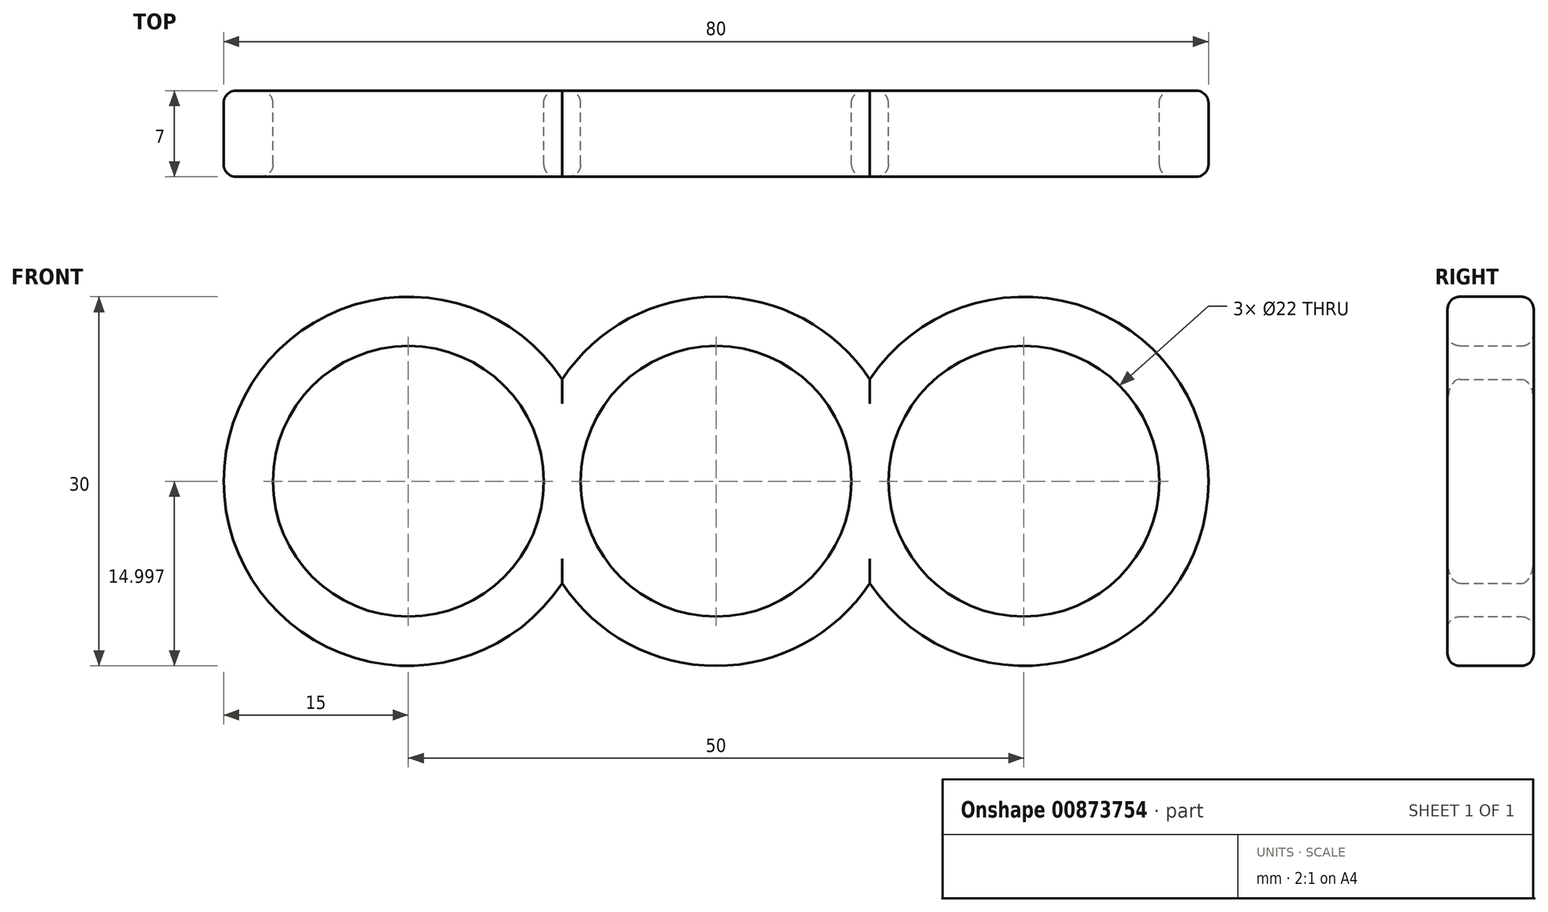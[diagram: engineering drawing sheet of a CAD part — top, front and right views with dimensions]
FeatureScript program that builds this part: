
annotation { "Feature Type Name" : "Feature", "Feature Type Description" : "" }
export const myFeature = defineFeature(function(context is Context, id is Id, definition is map)
    precondition{}
    {
        {
            var Q0;
            Q0=qCreatedBy(makeId("Front.planeOp"),FACE);
            var sketch = newSketch(context, id + "F0", { "sketchPlane" : qUnion([Q0])});
            skArc(sketch, "E0", {"start": v(0, 51.39) * mm, "mid": v(-11, 40.39) * mm, "end": v(0, 29.39) * mm});
            skArc(sketch, "E1", {"start": v(-12.5, 32.1) * mm, "mid": v(-7.1, 27.17) * mm, "end": v(0, 25.39) * mm});
            skCircle(sketch, "E2", {"center": v(-25, 40.39) * mm, "radius": 11 * mm});
            skArc(sketch, "E3", {"start": v(-12.5, 48.68) * mm, "mid": v(-40, 40.39) * mm, "end": v(-12.5, 32.1) * mm});
            skArc(sketch, "E4.trimOffspring", {"start": v(0, 55.39) * mm, "mid": v(-7.1, 53.6) * mm, "end": v(-12.5, 48.68) * mm});
            skArc(sketch, "E5.MirrorCS", {"start": v(0, 51.39) * mm, "mid": v(11, 40.39) * mm, "end": v(0, 29.39) * mm});
            skArc(sketch, "E6.MirrorCS", {"start": v(12.5, 32.1) * mm, "mid": v(7.1, 27.17) * mm, "end": v(0, 25.39) * mm});
            skArc(sketch, "E7.MirrorCS", {"start": v(0, 55.39) * mm, "mid": v(7.1, 53.6) * mm, "end": v(12.5, 48.68) * mm});
            skArc(sketch, "E8.MirrorCS", {"start": v(12.5, 48.68) * mm, "mid": v(40, 40.39) * mm, "end": v(12.5, 32.1) * mm});
            skCircle(sketch, "E9.MirrorC", {"center": v(25, 40.39) * mm, "radius": 11 * mm});
            skSolve(sketch);
        }
        {
            var Q0;
            Q0 = qSketchRegion(id + "F0", true);
            extrude(context, id + "F1", {"entities" : qUnion([Q0]), "depth" : 7 * mm, "offsetDistance" : 25 * mm});
        }
        {
            var Q0;
            Q0=makeQuery(id+"F1.opExtrude","CAP_FACE",FACE,{"disambiguationData":[OSD([sQuery(id+"F0.wireOp",EDGE,"E0"),sQuery(id+"F0.wireOp",EDGE,"E1"),sQuery(id+"F0.wireOp",EDGE,"E2"),sQuery(id+"F0.wireOp",EDGE,"E3"),sQuery(id+"F0.wireOp",EDGE,"E4.trimOffspring"),sQuery(id+"F0.wireOp",EDGE,"E5.MirrorCS"),sQuery(id+"F0.wireOp",EDGE,"E6.MirrorCS"),sQuery(id+"F0.wireOp",EDGE,"E7.MirrorCS"),sQuery(id+"F0.wireOp",EDGE,"E8.MirrorCS"),sQuery(id+"F0.wireOp",EDGE,"E9.MirrorC")])],"isStart":false});
            var Q1;
            Q1=makeQuery(id+"F1.opExtrude","CAP_FACE",FACE,{"disambiguationData":[OSD([sQuery(id+"F0.wireOp",EDGE,"E0"),sQuery(id+"F0.wireOp",EDGE,"E1"),sQuery(id+"F0.wireOp",EDGE,"E2"),sQuery(id+"F0.wireOp",EDGE,"E3"),sQuery(id+"F0.wireOp",EDGE,"E4.trimOffspring"),sQuery(id+"F0.wireOp",EDGE,"E5.MirrorCS"),sQuery(id+"F0.wireOp",EDGE,"E6.MirrorCS"),sQuery(id+"F0.wireOp",EDGE,"E7.MirrorCS"),sQuery(id+"F0.wireOp",EDGE,"E8.MirrorCS"),sQuery(id+"F0.wireOp",EDGE,"E9.MirrorC")])],"isStart":true});
            fillet(context, id + "F2", {"entities" : qUnion([Q0, Q1]), "radius" : 1 * mm, "tangentPropagation" : true, "allowEdgeOverflow" : false});
        }
    });
